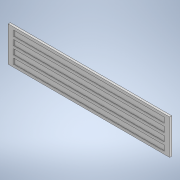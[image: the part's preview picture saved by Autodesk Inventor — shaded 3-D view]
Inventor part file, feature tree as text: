
AUTODESK INVENTOR PART (.ipt)
format: ipt  version: 2020.2 (Build 242310000, 310)  size: 129,536 bytes
history: native  units: mm
features: extrude x2, sketch x2
ambient origin geometry x8: Origin, YZ Plane, XZ Plane, XY Plane, X Axis, Y Axis, Z Axis, Center Point
bodies: Solide1 (feature_tree)
feature tree (4):
  extrude  "Extrusion1"  Depth=300.0mm
  extrude  "Extrusion2"  Depth=65.0mm
  sketch  "Esquisse1"
  sketch  "Esquisse2"
